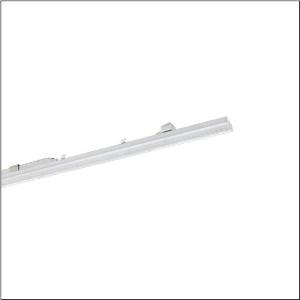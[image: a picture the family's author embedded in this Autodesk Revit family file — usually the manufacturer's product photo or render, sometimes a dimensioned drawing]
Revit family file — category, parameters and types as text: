
# Revit family: tl_l_5wd7a8h0h2b5
name_source: partatom
category: Lighting Fixtures
units: mm (PartAtom-declared; Revit-internal decimal feet)

## family parameters
Cut with Voids When Loaded = No
Host = Face
Light Source = No
Part Type = Normal
Room Calculation Point = No
Round Connector Dimension = Use Diameter
Shared = No

## types (1)
- --- (1 x LED, 850 lm, 4.5 W, 4000K)
    Apparent Load = 5 VA
    CIE Flux Codes = 49 84 98 100 100
    Color Rendering = 80
    Color Temperature = 4000K
    Default Elevation = 1800 mm
    Description = TL L, luminaire insert, of sheet steel, galvanised, coil coated, white, length: 1.500mm, width: 66mm, height: 67mm, surge protection,LED rated luminous flux: 4.990lm, light colour: 840, control gear: emergency light, with terminal, 3-pole, mains connection: 230..240V, AC, 50/60Hz, rated input power: 34W, micro fuse,primary optical cover: cover, of PMMA, light emission: direct distribution, protection rating (complete): as luminaire, insulation class (complete): insulation class I (protective earthing), certification: CE, impact resistance: IK06, permissible ambient temperature for indoor applications: +5..+35°C, packaging unit: 1 piece
    Height = 120 mm
    Lamp = 1 x LED
    Lamp Light Flux = 850 lm
    Lamp Power = 4.5 W
    Lamp count = 1
    Length = 1690 mm
    Luminous efficacy = 189 lm/W
    Manufacturer = Siteco
    ModVariant = No
    Model = 5WD7A8H0H2B5
    Mounting Place = Ceiling
    Mounting Type = Pendant
    Number of Poles = 1
    OnlyDefault = Yes
    Power Factor = 1
    Product Name = TL L
    Product group = luminaire insert
    ProductGroupID = 901
    Protection Class = Protection class I
    Protection Degree = Degree of protection
    RLX_Detail_Level = 1
    RLX_Emergency_Light_Flux = 0 lm
    RLX_Emergency_Type = 0
    RLX_Emergency_Type_DB = No
    RlxData = <blob elided: 17385 chars, md5=b4c95902>
    Socket = socket
    Standby Power = 0 W
    System Light Flux = 850 lm
    System Power = 5 W
    Type Comments = : emergency light operation: 3 h
    Type Image = l_1294382.jpg
    URL = http://relux.com
    VarID = @adj_012047
    Voltage = 0 V
    Weight = 0.00 kg
    Width = 208 mm

## geometry (parser evidence)
native form markers: Blend x4, Sweep x11
no freeform markers — native parametric forms only
